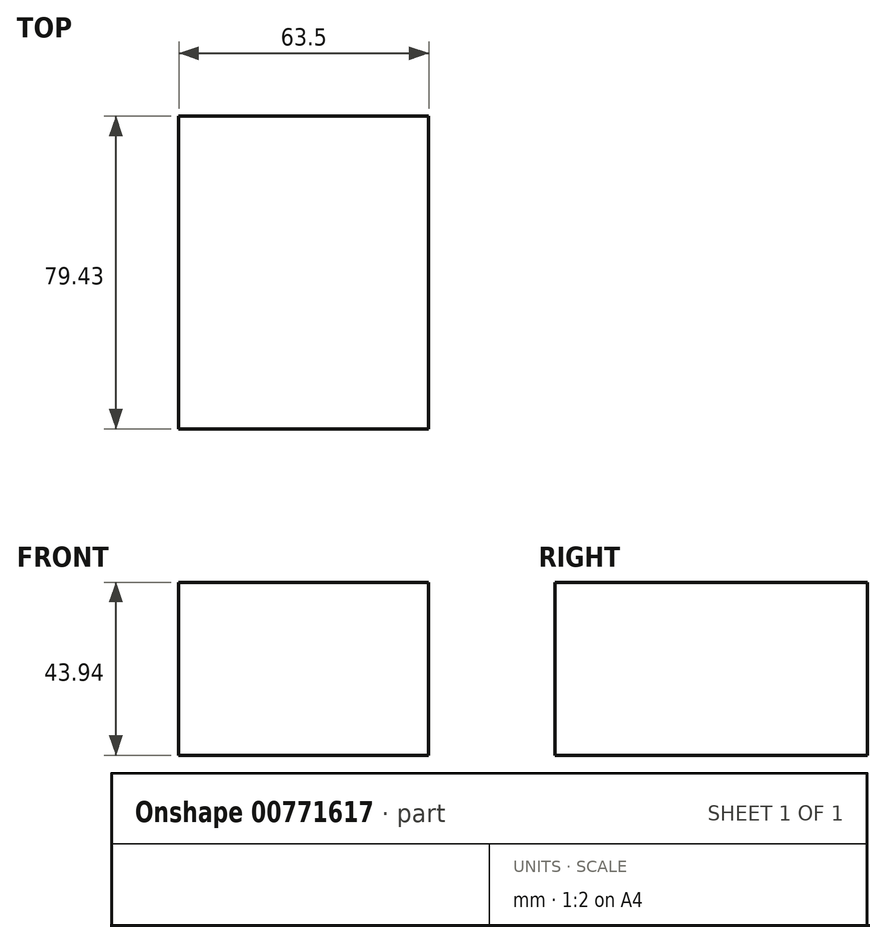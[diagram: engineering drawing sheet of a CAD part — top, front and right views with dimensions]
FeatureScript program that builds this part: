
annotation { "Feature Type Name" : "Feature", "Feature Type Description" : "" }
export const myFeature = defineFeature(function(context is Context, id is Id, definition is map)
    precondition{}
    {
        {
            var Q0;
            Q0=qCreatedBy(makeId("Front.planeOp"),FACE);
            var sketch = newSketch(context, id + "F0", { "sketchPlane" : qUnion([Q0])});
            skLineSegment(sketch, "E0.bottom", {"start": v(4.45, -2.74) * mm, "end": v(67.95, -2.74) * mm});
            skLineSegment(sketch, "E0.top", {"start": v(4.45, 41.2) * mm, "end": v(67.95, 41.2) * mm});
            skLineSegment(sketch, "E0.left", {"start": v(4.45, -2.74) * mm, "end": v(4.45, 41.2) * mm});
            skLineSegment(sketch, "E0.right", {"start": v(67.95, -2.74) * mm, "end": v(67.95, 41.2) * mm});
            skSolve(sketch);
        }
        {
            var Q0;
            Q0 = qSketchRegion(id + "F0", true);
            extrude(context, id + "F1", {"entities" : qUnion([Q0]), "depth" : 79.43 * mm, "offsetDistance" : 25.4 * mm});
        }
    });
